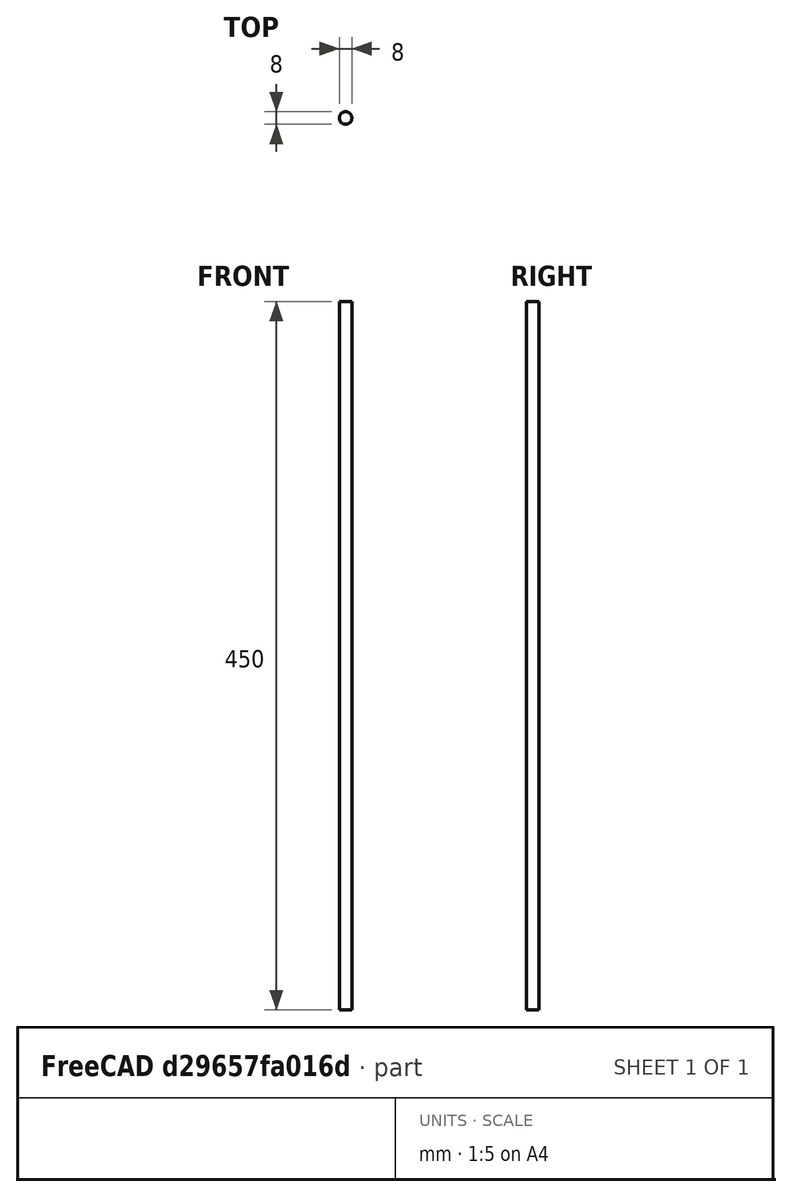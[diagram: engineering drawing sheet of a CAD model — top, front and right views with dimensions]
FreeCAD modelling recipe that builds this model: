
FCSTD DOCUMENT  (FreeCAD 0.19R)
Label: rod_threaded_8mm
License: All rights reserved
LicenseURL: http://en.wikipedia.org/wiki/All_rights_reserved
objects: PartDesign::CoordinateSystem×2, Sketcher::SketchObject×1, PartDesign::Pad×1, PartDesign::Body×1
note: 6 computed .brp shape members not serialized (recipe doc carries the construction recipe); baked Part::Feature solids carry a one-line shape summary decoded from their .brp

FEATURE [Sketcher::SketchObject] Sketch
  FullyConstrained = true
  MapMode = 5
  Support = -> [XY_Plane]
  sketch-geometry (1):
    g0: Circle CenterX=0 CenterY=0 CenterZ=0 NormalX=0 NormalY=0 NormalZ=1 AngleXU=0 Radius=4
  constraints (2):
    c: Coincident(g0,g-1)
    c: Diameter(g0) = 8
FEATURE [PartDesign::Pad] Pad
  Direction = (1,1,1)
  Length = 450
  Length2 = 100
  Profile = -> Sketch
  Refine = true
  Type = 0
FEATURE [PartDesign::CoordinateSystem] Local_CS
  AttacherType = Attacher::AttachEngine3D
  MapMode = 11
  Placement = pos=(0,0,0) rot=(0,0,1;1.5708rad)
  Support = -> [Pad]
FEATURE [PartDesign::CoordinateSystem] Local_CS001
  AttacherType = Attacher::AttachEngine3D
  MapMode = 11
  Placement = pos=(0,0,450) rot=(0,0,1;1.5708rad)
  Support = -> [Pad]
FEATURE [PartDesign::Body] Body
  Group = -> [Sketch,Pad,Local_CS,Local_CS001]
  Origin = -> Origin
  Tip = -> Pad
